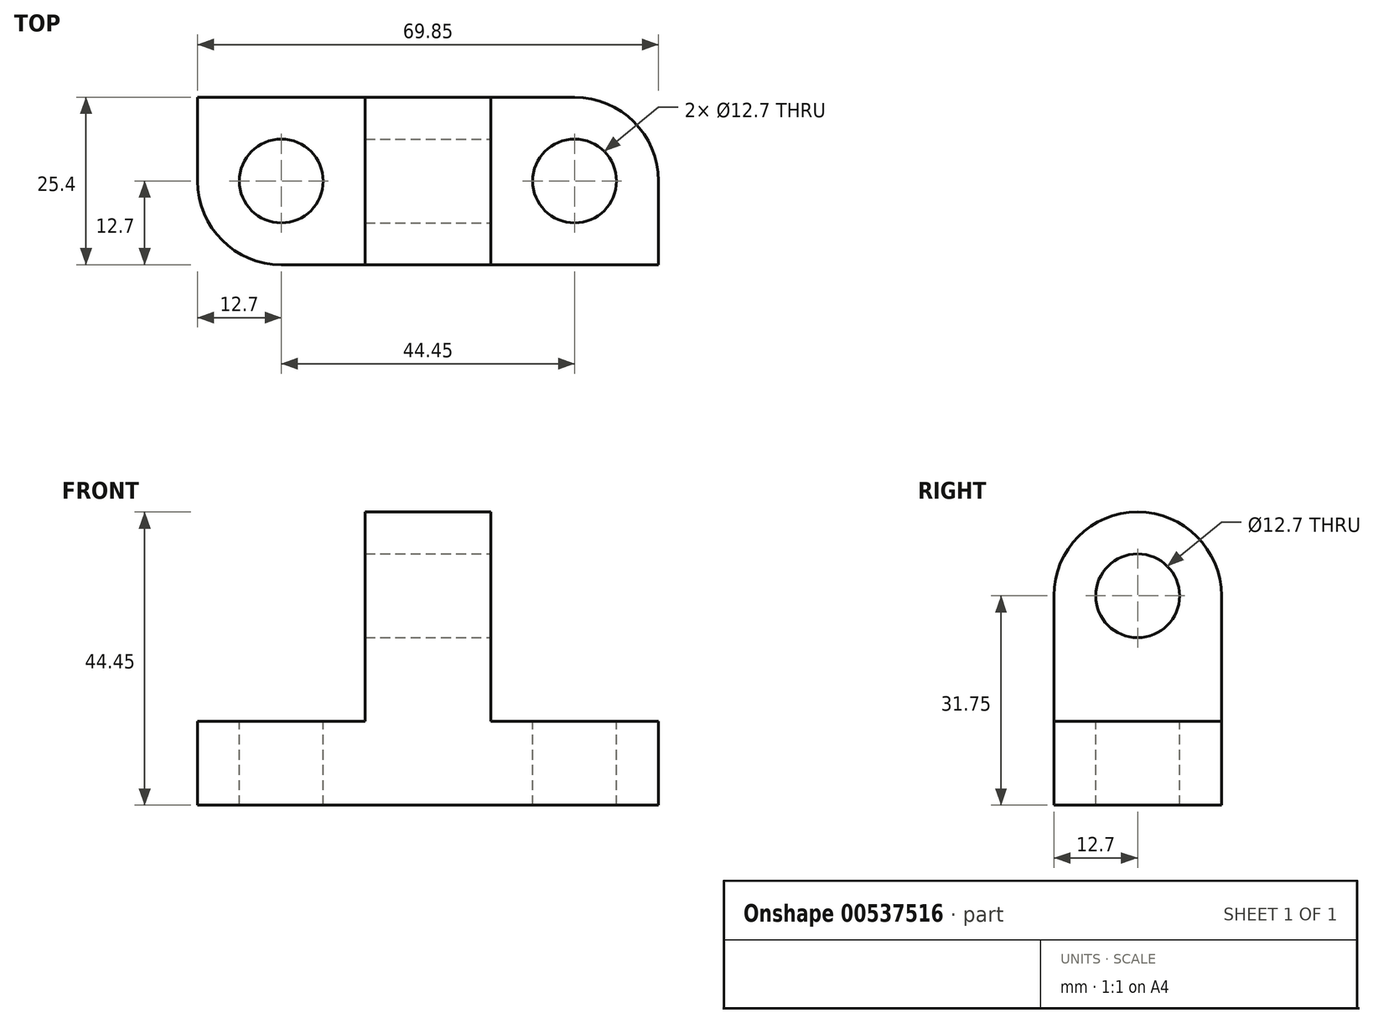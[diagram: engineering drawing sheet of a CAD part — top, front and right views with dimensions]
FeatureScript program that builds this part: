
annotation { "Feature Type Name" : "Feature", "Feature Type Description" : "" }
export const myFeature = defineFeature(function(context is Context, id is Id, definition is map)
    precondition{}
    {
        {
            var Q0;
            Q0=qCreatedBy(makeId("Front.planeOp"),FACE);
            var sketch = newSketch(context, id + "F0", { "sketchPlane" : qUnion([Q0])});
            skLineSegment(sketch, "E0", {"start": v(0, 0) * mm, "end": v(69.85, 0) * mm});
            skLineSegment(sketch, "E1", {"start": v(69.85, 0) * mm, "end": v(69.85, 44.45) * mm});
            skLineSegment(sketch, "E2", {"start": v(69.85, 44.45) * mm, "end": v(0, 44.45) * mm});
            skLineSegment(sketch, "E3", {"start": v(0, 44.45) * mm, "end": v(0, 0) * mm});
            skSolve(sketch);
        }
        {
            var Q0;
            Q0 = qSketchRegion(id + "F0", true);
            extrude(context, id + "F1", {"entities" : qUnion([Q0]), "depth" : 25.4 * mm, "offsetDistance" : 25.4 * mm});
        }
        {
            var Q0;
            Q0=makeQuery(id+"F1.opExtrude","CAP_FACE",FACE,{"disambiguationData":[OSD([sQuery(id+"F0.wireOp",EDGE,"E0"),sQuery(id+"F0.wireOp",EDGE,"E1"),sQuery(id+"F0.wireOp",EDGE,"E2"),sQuery(id+"F0.wireOp",EDGE,"E3")])],"isStart":false});
            var sketch = newSketch(context, id + "F2", { "sketchPlane" : qUnion([Q0])});
            skLineSegment(sketch, "E4", {"start": v(0, 12.7) * mm, "end": v(25.4, 12.7) * mm});
            skLineSegment(sketch, "E5", {"start": v(25.4, 12.7) * mm, "end": v(25.4, 44.45) * mm});
            skLineSegment(sketch, "E6", {"start": v(25.4, 44.45) * mm, "end": v(44.45, 44.45) * mm});
            skLineSegment(sketch, "E7", {"start": v(44.45, 44.45) * mm, "end": v(44.45, 12.7) * mm});
            skLineSegment(sketch, "E8", {"start": v(44.45, 12.7) * mm, "end": v(69.85, 12.7) * mm});
            skSolve(sketch);
        }
        {
            var Q0;
            Q0 = qSketchRegion(id + "F2", true);
            var Q1;
            {var subQ0=sQuery(id+"F2.wireOp",EDGE,"E4");Q1=makeQuery(id+"F2.imprint","IMPRINT",FACE,{"disambiguationData":[TD([[makeQuery(id+"F2.imprint","IMPRINT",EDGE,{"derivedFrom":subQ0}),1.0]])]});}
            var Q2;
            {var subQ0=sQuery(id+"F2.wireOp",EDGE,"E7");Q2=makeQuery(id+"F2.imprint","IMPRINT",FACE,{"disambiguationData":[TD([[makeQuery(id+"F2.imprint","IMPRINT",EDGE,{"derivedFrom":subQ0}),1.0]])]});}
            extrude(context, id + "F3", {"entities" : qUnion([Q0, Q1, Q2]), "operationType" : NewBodyOperationType.REMOVE, "oppositeDirection" : true, "depth" : 25.4 * mm, "offsetDistance" : 25.4 * mm});
        }
        {
            var Q0;
            Q0=makeQuery(id+"F3.boolean.opBoolean","COPY",FACE,{"derivedFrom":makeQuery(id+"F3.opExtrude","SWEPT_FACE",FACE,{"disambiguationData":[OSD([sQuery(id+"F2.wireOp",EDGE,"E4")])]})});
            var sketch = newSketch(context, id + "F4", { "sketchPlane" : qUnion([Q0])});
            skCircle(sketch, "E9", {"center": v(12.7, -12.7) * mm, "radius": 6.35 * mm});
            skPoint(sketch, "E9.centerSnap0", {"position": v(12.7, 0) * mm});
            skArc(sketch, "E10", {"start": v(12.7, 0) * mm, "mid": v(0, -12.7) * mm, "end": v(12.7, -25.4) * mm});
            skLineSegment(sketch, "E11", {"start": v(12.7, -25.4) * mm, "end": v(0, -25.4) * mm});
            skLineSegment(sketch, "E12", {"start": v(0, -25.4) * mm, "end": v(0, -12.7) * mm});
            skSolve(sketch);
        }
        {
            var Q0;
            Q0=makeQuery(id+"F4.imprint","IMPRINT",FACE,{"disambiguationData":[TD([[makeQuery(id+"F4.imprint","IMPRINT",EDGE,{"derivedFrom":sQuery(id+"F4.wireOp",EDGE,"E9")}),1.0]])]});
            var Q1;
            {var subQ0=sQuery(id+"F4.wireOp",EDGE,"E10");var subQ1=sQuery(id+"F2.wireOp",EDGE,"E4");var subQ2=makeQuery(id+"F3.boolean.opBoolean","COPY",EDGE,{"derivedFrom":makeQuery(id+"F3.opExtrude","CAP_EDGE",EDGE,{"disambiguationData":[OSD([subQ1])],"isStart":false})});var subQ3=makeQuery(id+"F4.imprint","INTERSECT",VERTEX,{"derivedFrom":[subQ2,subQ0]});Q1=makeQuery(id+"F4.imprint","IMPRINT",FACE,{"disambiguationData":[TD([[makeQuery(id+"F4.imprint","IMPRINT",EDGE,{"disambiguationData":[TD([[subQ3,1.0]])],"derivedFrom":subQ2}),-1.0]])]});}
            var Q2;
            {var subQ0=sQuery(id+"F4.wireOp",EDGE,"E11");Q2=makeQuery(id+"F4.imprint","IMPRINT",FACE,{"disambiguationData":[TD([[makeQuery(id+"F4.imprint","IMPRINT",EDGE,{"derivedFrom":subQ0}),1.0]])]});}
            extrude(context, id + "F5", {"entities" : qUnion([Q0, Q1, Q2]), "operationType" : NewBodyOperationType.REMOVE, "oppositeDirection" : true, "depth" : 12.7 * mm, "offsetDistance" : 25.4 * mm});
        }
        {
            var Q0;
            Q0=makeQuery(id+"F3.boolean.opBoolean","COPY",FACE,{"derivedFrom":makeQuery(id+"F3.opExtrude","SWEPT_FACE",FACE,{"disambiguationData":[OSD([sQuery(id+"F2.wireOp",EDGE,"E8")])]})});
            var sketch = newSketch(context, id + "F6", { "sketchPlane" : qUnion([Q0])});
            skCircle(sketch, "E13", {"center": v(57.15, -12.7) * mm, "radius": 6.35 * mm});
            skPoint(sketch, "E13.centerSnap0", {"position": v(57.15, 0) * mm});
            skArc(sketch, "E14", {"start": v(57.15, -25.4) * mm, "mid": v(69.85, -12.7) * mm, "end": v(57.15, 0) * mm});
            skLineSegment(sketch, "E15", {"start": v(69.85, -12.7) * mm, "end": v(69.85, 0) * mm});
            skSolve(sketch);
        }
        {
            var Q0;
            Q0=makeQuery(id+"F6.imprint","IMPRINT",FACE,{"disambiguationData":[TD([[makeQuery(id+"F6.imprint","IMPRINT",EDGE,{"derivedFrom":sQuery(id+"F6.wireOp",EDGE,"E13")}),1.0]])]});
            var Q1;
            {var subQ4=sQuery(id+"F6.wireOp",EDGE,"E15");Q1=makeQuery(id+"F6.imprint","IMPRINT",FACE,{"disambiguationData":[TD([[makeQuery(id+"F6.imprint","IMPRINT",EDGE,{"derivedFrom":subQ4}),-1.0]])]});}
            var Q2;
            {var subQ0=sQuery(id+"F6.wireOp",EDGE,"E14");var subQ1=sQuery(id+"F2.wireOp",EDGE,"E8");var subQ2=makeQuery(id+"F3.boolean.opBoolean","COPY",EDGE,{"derivedFrom":makeQuery(id+"F3.opExtrude","CAP_EDGE",EDGE,{"disambiguationData":[OSD([subQ1])],"isStart":true})});var subQ3=makeQuery(id+"F6.imprint","INTERSECT",VERTEX,{"derivedFrom":[subQ2,subQ0]});Q2=makeQuery(id+"F6.imprint","IMPRINT",FACE,{"disambiguationData":[TD([[makeQuery(id+"F6.imprint","IMPRINT",EDGE,{"disambiguationData":[TD([[subQ3,-1.0]])],"derivedFrom":subQ2}),1.0]])]});}
            extrude(context, id + "F7", {"entities" : qUnion([Q0, Q1, Q2]), "operationType" : NewBodyOperationType.REMOVE, "oppositeDirection" : true, "depth" : 12.7 * mm, "offsetDistance" : 25.4 * mm});
        }
        {
            var Q0;
            Q0=makeQuery(id+"F3.boolean.opBoolean","COPY",FACE,{"derivedFrom":makeQuery(id+"F3.opExtrude","SWEPT_FACE",FACE,{"disambiguationData":[OSD([sQuery(id+"F2.wireOp",EDGE,"E7")])]})});
            var sketch = newSketch(context, id + "F8", { "sketchPlane" : qUnion([Q0])});
            skCircle(sketch, "E16", {"center": v(-12.7, 31.75) * mm, "radius": 6.35 * mm});
            skPoint(sketch, "E16.centerSnap0", {"position": v(-12.7, 44.45) * mm});
            skArc(sketch, "E17", {"start": v(0, 31.75) * mm, "mid": v(-12.7, 44.45) * mm, "end": v(-25.4, 31.75) * mm});
            skSolve(sketch);
        }
        {
            var Q0;
            Q0=makeQuery(id+"F8.imprint","IMPRINT",FACE,{"disambiguationData":[TD([[makeQuery(id+"F8.imprint","IMPRINT",EDGE,{"derivedFrom":sQuery(id+"F8.wireOp",EDGE,"E16")}),1.0]])]});
            var Q1;
            {var subQ0=sQuery(id+"F8.wireOp",EDGE,"E17");var subQ1=sQuery(id+"F2.wireOp",EDGE,"E7");var subQ2=makeQuery(id+"F3.boolean.opBoolean","COPY",EDGE,{"derivedFrom":makeQuery(id+"F3.opExtrude","CAP_EDGE",EDGE,{"disambiguationData":[OSD([subQ1])],"isStart":true})});var subQ3=makeQuery(id+"F8.imprint","INTERSECT",VERTEX,{"derivedFrom":[subQ2,subQ0]});Q1=makeQuery(id+"F8.imprint","IMPRINT",FACE,{"disambiguationData":[TD([[makeQuery(id+"F8.imprint","IMPRINT",EDGE,{"disambiguationData":[TD([[subQ3,1.0]])],"derivedFrom":subQ0}),-1.0]])]});}
            var Q2;
            {var subQ0=sQuery(id+"F8.wireOp",EDGE,"E17");var subQ1=sQuery(id+"F2.wireOp",EDGE,"E7");var subQ2=makeQuery(id+"F3.boolean.opBoolean","COPY",EDGE,{"derivedFrom":makeQuery(id+"F3.opExtrude","CAP_EDGE",EDGE,{"disambiguationData":[OSD([subQ1])],"isStart":false})});var subQ3=makeQuery(id+"F8.imprint","INTERSECT",VERTEX,{"derivedFrom":[subQ2,subQ0]});Q2=makeQuery(id+"F8.imprint","IMPRINT",FACE,{"disambiguationData":[TD([[makeQuery(id+"F8.imprint","IMPRINT",EDGE,{"disambiguationData":[TD([[subQ3,-1.0]])],"derivedFrom":subQ0}),-1.0]])]});}
            extrude(context, id + "F9", {"entities" : qUnion([Q0, Q1, Q2]), "operationType" : NewBodyOperationType.REMOVE, "oppositeDirection" : true, "depth" : 25.4 * mm, "offsetDistance" : 25.4 * mm});
        }
    });
